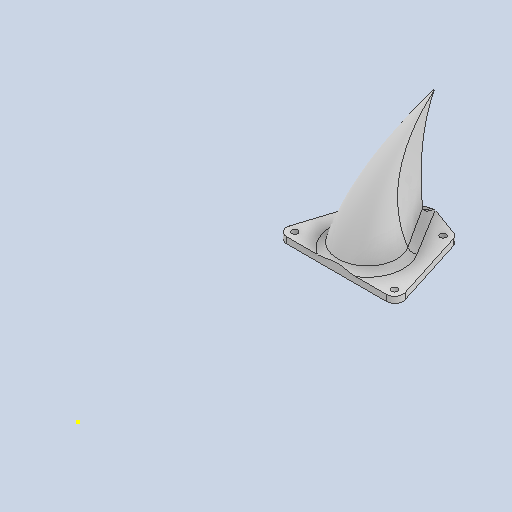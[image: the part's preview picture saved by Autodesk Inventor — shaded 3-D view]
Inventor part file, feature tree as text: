
AUTODESK INVENTOR PART (.ipt)
format: ipt  version: 2023 (Build 270158000, 158)  size: 429,568 bytes
history: native  units: in
note: dims shown in document units (in); Inventor stores cm internally (conversion verified against a paired STEP export)
features: sketch x6, plane x2, extrude x1, loft x1, fillet x1
ambient origin geometry x8: Origin, YZ Plane, XZ Plane, XY Plane, X Axis, Y Axis, Z Axis, Center Point
bodies: Solid1 (feature_tree)
feature tree (11):
  extrude  "Extrusion1"  Depth=0.1181in TaperAngle=0.0deg
  sketch  "Sketch2"  dims[d3=1.9685in d4=0.5906in d11=0.9843in]
  sketch  "Sketch3"  dims[d12=0.2953in]
  plane  "Work Plane1"
  sketch  "Sketch4"  dims[d21=0.0197in]
  plane  "Work Plane2"
  loft  "Loft3"
  fillet  "Fillet1"  Radius=0.9843in
  sketch  "Sketch6"  dims[d24=0.0in d25=90.0deg d26=0.0in d27=90.0deg d28=0.1339in]
  sketch  "Sketch1"  dims[d0=0.1181in d1=0.1181in d2=0.0in]
  sketch  "Sketch5"  dims[d22=0.0in d23=90.0deg]
